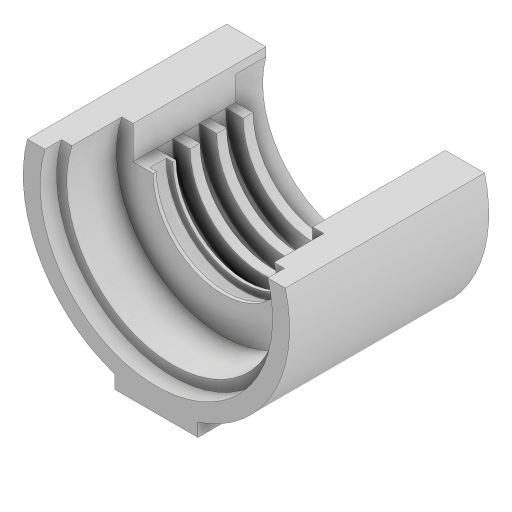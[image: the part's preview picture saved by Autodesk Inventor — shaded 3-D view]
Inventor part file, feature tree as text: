
AUTODESK INVENTOR PART (.ipt)
format: ipt  version: 2023 (Build 270158000, 158)  size: 275,968 bytes
history: native  units: mm
features: sketch x4, extrude x3, revolve x1
ambient origin geometry x8: Origin, YZ Plane, XZ Plane, XY Plane, X Axis, Y Axis, Z Axis, Center Point
bodies: Solid1 (feature_tree)
feature tree (8):
  revolve  "Revolution1"  [1 undecoded]
  extrude  "Extrusion1"  Depth=5.0mm
  extrude  "Extrusion2"  Depth=3.0mm
  extrude  "Extrusion3"  Depth=3.0mm
  sketch  "Sketch1"  dims[d2=35.1mm d4=3.0mm]
  sketch  "Sketch2"  dims[d6=23.0mm d7=5.0mm]
  sketch  "Sketch3"  dims[d8=5.0mm d11=3.0mm]
  sketch  "Sketch4"  dims[d12=5.0mm d13=3.0mm d14=5.0mm d15=3.0mm d16=2.0mm d17=1.0mm d18=1.0mm d19=28.0mm d20=27.0mm d21=27.0mm d22=23.0mm d23=90.0deg d24=10.0mm d25=0.0mm d26=0.0mm d27=0.0mm d28=15.0mm d29=5.0mm d30=32.0mm d31=10.0mm d32=0.0mm]
note: 1 required parameter value undecoded (feature->parameter linkage not recoverable at this tier; creation-order binding heuristic only, values carry confidence <= 0.55)
